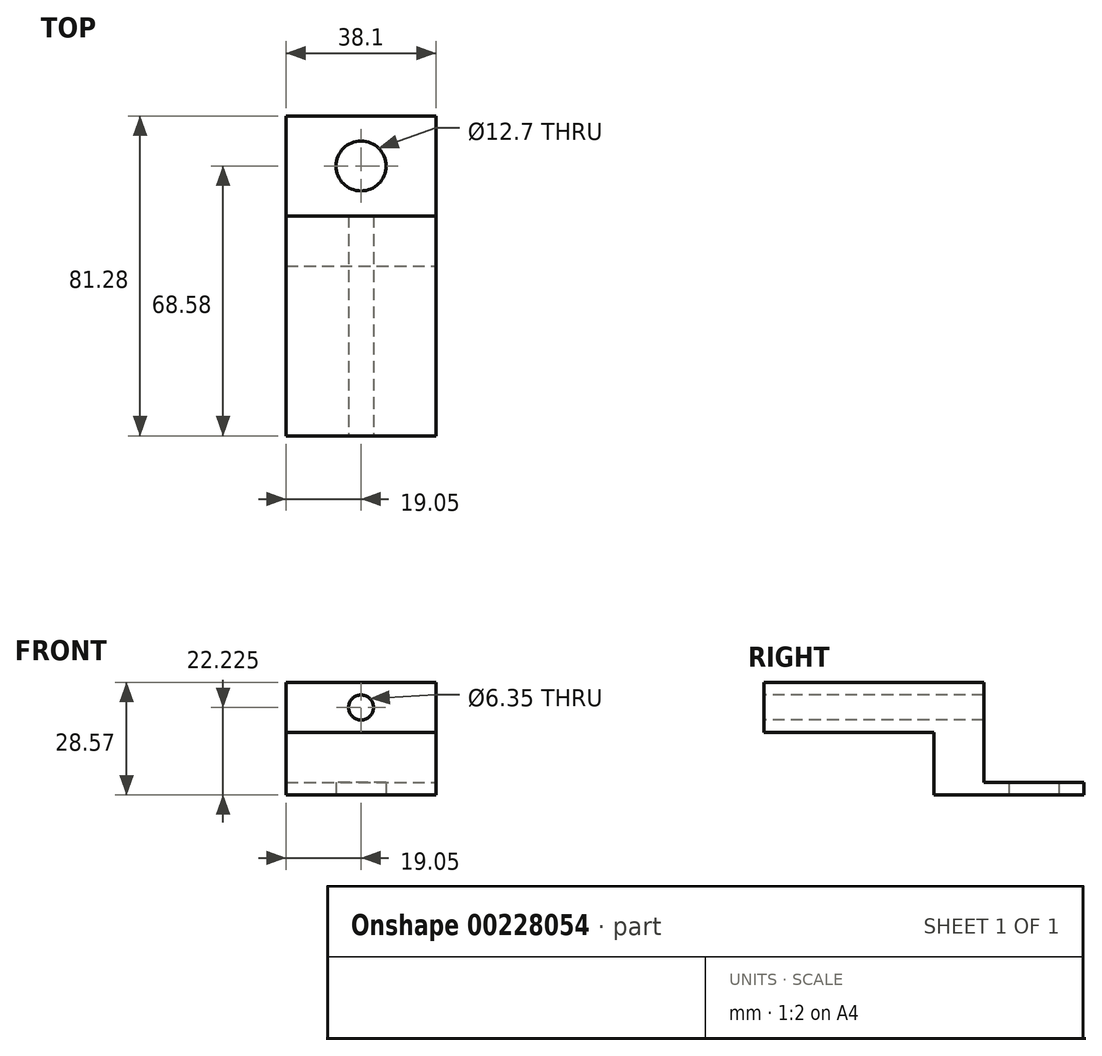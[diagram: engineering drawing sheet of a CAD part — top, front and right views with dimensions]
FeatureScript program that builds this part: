
annotation { "Feature Type Name" : "Feature", "Feature Type Description" : "" }
export const myFeature = defineFeature(function(context is Context, id is Id, definition is map)
    precondition{}
    {
        {
            var Q0;
            Q0=qCreatedBy(makeId("Top.planeOp"),FACE);
            var sketch = newSketch(context, id + "F0", { "sketchPlane" : qUnion([Q0])});
            skLineSegment(sketch, "E0.bottom", {"start": v(0, 0) * mm, "end": v(38.1, 0) * mm});
            skLineSegment(sketch, "E0.top", {"start": v(0, 38.1) * mm, "end": v(38.1, 38.1) * mm});
            skLineSegment(sketch, "E0.left", {"start": v(0, 0) * mm, "end": v(0, 38.1) * mm});
            skLineSegment(sketch, "E0.right", {"start": v(38.1, 0) * mm, "end": v(38.1, 38.1) * mm});
            skCircle(sketch, "E1", {"center": v(19.05, 25.4) * mm, "radius": 6.35 * mm});
            skLineSegment(sketch, "E2", {"start": v(19.05, 38.1) * mm, "end": v(19.05, 0) * mm, "construction": true});
            skSolve(sketch);
        }
        {
            var Q0;
            Q0 = qSketchRegion(id + "F0", true);
            extrude(context, id + "F1", {"entities" : qUnion([Q0]), "depth" : 3.17 * mm, "offsetDistance" : 25.4 * mm});
        }
        {
            var Q0;
            Q0=makeQuery(id+"F1.opExtrude","CAP_FACE",FACE,{"disambiguationData":[OSD([sQuery(id+"F0.wireOp",EDGE,"E0.bottom"),sQuery(id+"F0.wireOp",EDGE,"E0.top"),sQuery(id+"F0.wireOp",EDGE,"E0.left"),sQuery(id+"F0.wireOp",EDGE,"E0.right"),sQuery(id+"F0.wireOp",EDGE,"E1")])],"isStart":false});
            var sketch = newSketch(context, id + "F2", { "sketchPlane" : qUnion([Q0])});
            skLineSegment(sketch, "E3.bottom", {"start": v(0, 0) * mm, "end": v(38.1, 0) * mm});
            skLineSegment(sketch, "E3.top", {"start": v(0, 12.7) * mm, "end": v(38.1, 12.7) * mm});
            skLineSegment(sketch, "E3.left", {"start": v(0, 0) * mm, "end": v(0, 12.7) * mm});
            skLineSegment(sketch, "E3.right", {"start": v(38.1, 0) * mm, "end": v(38.1, 12.7) * mm});
            skSolve(sketch);
        }
        {
            var Q0;
            Q0 = qSketchRegion(id + "F2", true);
            extrude(context, id + "F3", {"entities" : qUnion([Q0]), "operationType" : NewBodyOperationType.ADD, "depth" : 25.4 * mm, "offsetDistance" : 25.4 * mm});
        }
        {
            var Q0;
            Q0=makeQuery(id+"F3.boolean.opBoolean","MERGE",FACE,{"derivedFrom":[makeQuery(id+"F1.opExtrude","SWEPT_FACE",FACE,{"disambiguationData":[OSD([sQuery(id+"F0.wireOp",EDGE,"E0.bottom")])]}),makeQuery(id+"F3.opExtrude","SWEPT_FACE",FACE,{"disambiguationData":[OSD([sQuery(id+"F2.wireOp",EDGE,"E3.bottom")])]})]});
            var sketch = newSketch(context, id + "F4", { "sketchPlane" : qUnion([Q0])});
            skLineSegment(sketch, "E4.bottom", {"start": v(0, 28.58) * mm, "end": v(38.1, 28.58) * mm});
            skLineSegment(sketch, "E4.top", {"start": v(0, 15.88) * mm, "end": v(38.1, 15.88) * mm});
            skLineSegment(sketch, "E4.left", {"start": v(0, 28.58) * mm, "end": v(0, 15.88) * mm});
            skLineSegment(sketch, "E4.right", {"start": v(38.1, 28.58) * mm, "end": v(38.1, 15.88) * mm});
            skSolve(sketch);
        }
        {
            var Q0;
            Q0 = qSketchRegion(id + "F4", true);
            extrude(context, id + "F5", {"entities" : qUnion([Q0]), "operationType" : NewBodyOperationType.ADD, "depth" : 43.18 * mm, "offsetDistance" : 25.4 * mm});
        }
        {
            var Q0;
            Q0=makeQuery(id+"F5.opExtrude","CAP_FACE",FACE,{"disambiguationData":[OSD([sQuery(id+"F4.wireOp",EDGE,"E4.bottom"),sQuery(id+"F4.wireOp",EDGE,"E4.top"),sQuery(id+"F4.wireOp",EDGE,"E4.left"),sQuery(id+"F4.wireOp",EDGE,"E4.right")])],"isStart":false});
            var sketch = newSketch(context, id + "F6", { "sketchPlane" : qUnion([Q0])});
            skCircle(sketch, "E5", {"center": v(19.05, 22.23) * mm, "radius": 3.18 * mm});
            skLineSegment(sketch, "E6", {"start": v(19.05, 28.58) * mm, "end": v(19.05, 15.88) * mm, "construction": true});
            skSolve(sketch);
        }
        {
            var Q0;
            Q0 = qSketchRegion(id + "F6", true);
            extrude(context, id + "F7", {"entities" : qUnion([Q0]), "operationType" : NewBodyOperationType.REMOVE, "endBound" : BoundingType.THROUGH_ALL, "oppositeDirection" : true, "depth" : 25.4 * mm, "offsetDistance" : 25.4 * mm});
        }
    });
